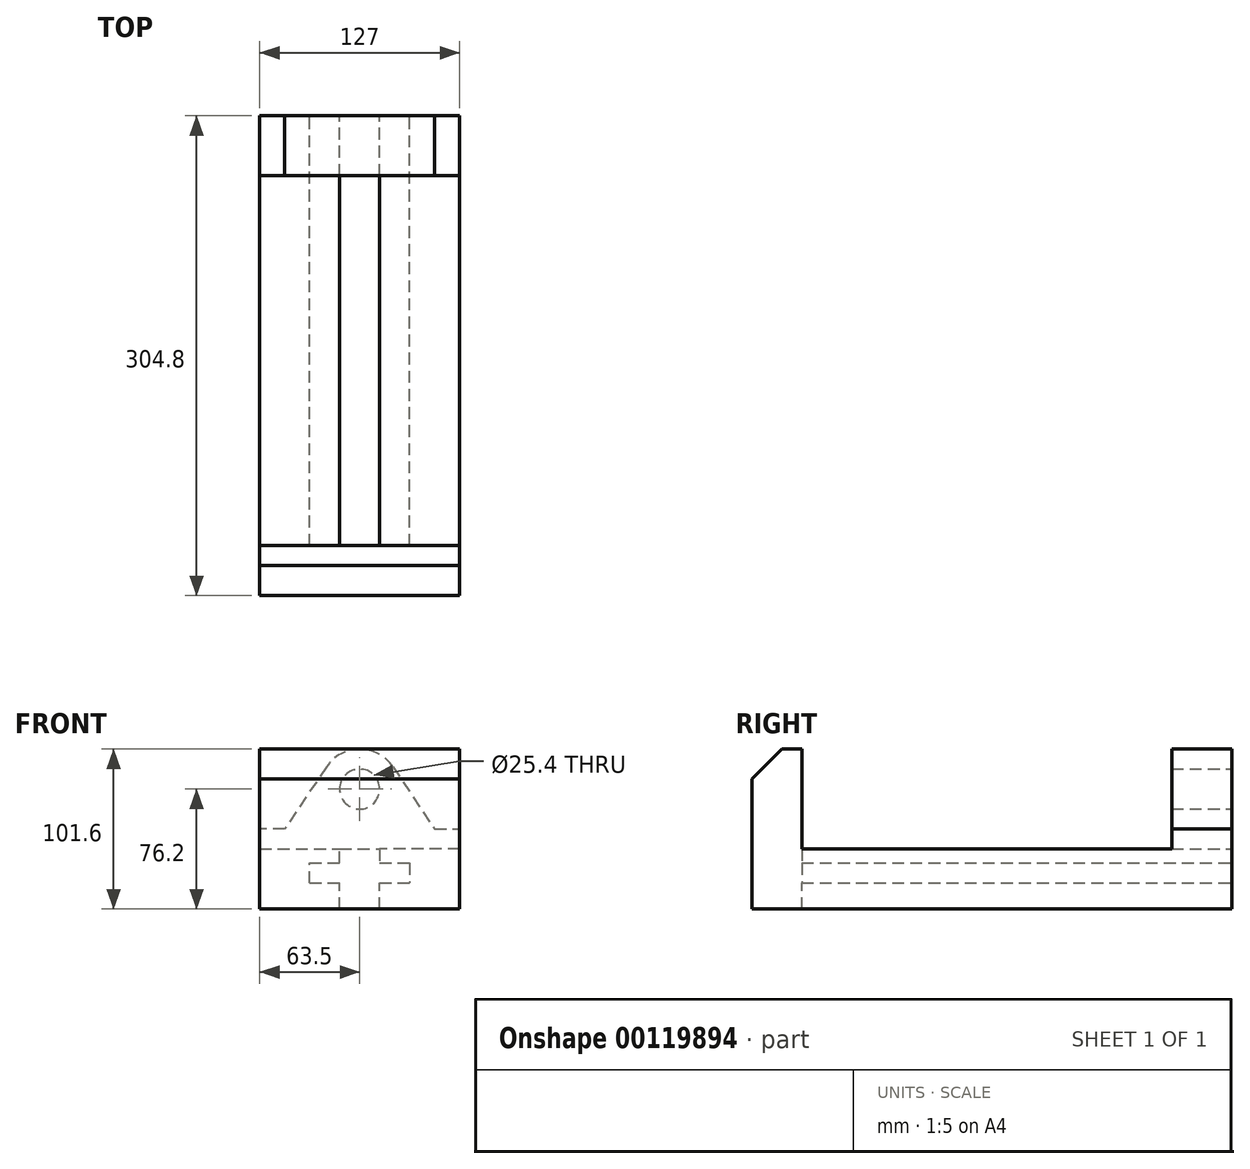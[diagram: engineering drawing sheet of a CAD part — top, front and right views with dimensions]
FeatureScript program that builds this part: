
annotation { "Feature Type Name" : "Feature", "Feature Type Description" : "" }
export const myFeature = defineFeature(function(context is Context, id is Id, definition is map)
    precondition{}
    {
        {
            var Q0;
            Q0=qCreatedBy(makeId("Front.planeOp"),FACE);
            var sketch = newSketch(context, id + "F0", { "sketchPlane" : qUnion([Q0])});
            skLineSegment(sketch, "E0.bottom", {"start": v(-63.5, 0) * mm, "end": v(63.5, 0) * mm});
            skLineSegment(sketch, "E0.left", {"start": v(-63.5, 0) * mm, "end": v(-63.5, 50.8) * mm});
            skLineSegment(sketch, "E0.right", {"start": v(63.5, 0) * mm, "end": v(63.5, 50.8) * mm});
            skPoint(sketch, "E1", {"position": v(0, 101.6) * mm});
            skArc(sketch, "E2", {"start": v(21.1, 90.35) * mm, "mid": v(0, 101.6) * mm, "end": v(-21.1, 90.35) * mm});
            skCircle(sketch, "E3", {"center": v(0, 76.2) * mm, "radius": 12.7 * mm});
            skLineSegment(sketch, "E4", {"start": v(21.1, 90.35) * mm, "end": v(47.62, 50.8) * mm});
            skLineSegment(sketch, "E5", {"start": v(47.62, 50.8) * mm, "end": v(63.5, 50.8) * mm});
            skLineSegment(sketch, "E6", {"start": v(-21.1, 90.35) * mm, "end": v(-47.62, 50.8) * mm});
            skLineSegment(sketch, "E7", {"start": v(-47.63, 50.8) * mm, "end": v(-63.5, 50.8) * mm});
            skLineSegment(sketch, "E8", {"start": v(0, 0) * mm, "end": v(0, 101.6) * mm});
            skSolve(sketch);
        }
        {
            var Q0;
            Q0 = qSketchRegion(id + "F0", true);
            extrude(context, id + "F1", {"entities" : qUnion([Q0]), "depth" : 38.1 * mm});
        }
        {
            var Q0;
            Q0=qCreatedBy(makeId("Right.planeOp"),FACE);
            var sketch = newSketch(context, id + "F2", { "sketchPlane" : qUnion([Q0])});
            skLineSegment(sketch, "E9.bottom", {"start": v(0, 0) * mm, "end": v(-304.8, 0) * mm});
            skLineSegment(sketch, "E9.top", {"start": v(0, 38.1) * mm, "end": v(-273.05, 38.1) * mm});
            skLineSegment(sketch, "E9.left", {"start": v(0, 0) * mm, "end": v(0, 38.1) * mm});
            skLineSegment(sketch, "E9.right", {"start": v(-304.8, 0) * mm, "end": v(-304.8, 82.55) * mm});
            skLineSegment(sketch, "E10", {"start": v(-38.1, 101.6) * mm, "end": v(0, 101.6) * mm, "construction": true});
            skPoint(sketch, "E11", {"position": v(-304.8, 38.1) * mm});
            skLineSegment(sketch, "E12", {"start": v(-304.8, 82.55) * mm, "end": v(-285.75, 101.6) * mm});
            skLineSegment(sketch, "E13", {"start": v(-285.75, 101.6) * mm, "end": v(-273.05, 101.6) * mm});
            skLineSegment(sketch, "E14", {"start": v(-273.05, 101.6) * mm, "end": v(-273.05, 38.1) * mm});
            skSolve(sketch);
        }
        {
            var Q0;
            Q0 = qSketchRegion(id + "F2", true);
            extrude(context, id + "F3", {"entities" : qUnion([Q0]), "operationType" : NewBodyOperationType.ADD, "oppositeDirection" : true, "depth" : 63.5 * mm, "hasSecondDirection" : true, "secondDirectionOppositeDirection" : false, "secondDirectionDepth" : 63.5 * mm});
        }
        {
            var Q0;
            Q0=qCreatedBy(makeId("Front.planeOp"),FACE);
            var sketch = newSketch(context, id + "F4", { "sketchPlane" : qUnion([Q0])});
            skLineSegment(sketch, "E15.bottom", {"start": v(-12.7, 0) * mm, "end": v(12.7, 0) * mm});
            skLineSegment(sketch, "E15.left", {"start": v(-12.7, 0) * mm, "end": v(-12.7, 16.51) * mm});
            skLineSegment(sketch, "E15.right", {"start": v(12.7, 0) * mm, "end": v(12.7, 16.51) * mm});
            skLineSegment(sketch, "E16", {"start": v(-31.75, 16.51) * mm, "end": v(-12.7, 16.51) * mm});
            skLineSegment(sketch, "E17.trimOffspring", {"start": v(12.7, 16.51) * mm, "end": v(31.75, 16.51) * mm});
            skLineSegment(sketch, "E18", {"start": v(-31.75, 16.51) * mm, "end": v(-31.75, 29.21) * mm});
            skLineSegment(sketch, "E19", {"start": v(-31.75, 29.21) * mm, "end": v(-12.7, 29.21) * mm});
            skLineSegment(sketch, "E20", {"start": v(-12.7, 29.21) * mm, "end": v(-12.7, 38.1) * mm});
            skLineSegment(sketch, "E21", {"start": v(-12.7, 38.1) * mm, "end": v(12.7, 38.1) * mm});
            skLineSegment(sketch, "E22", {"start": v(12.7, 38.1) * mm, "end": v(12.7, 29.2) * mm});
            skLineSegment(sketch, "E23", {"start": v(12.7, 29.2) * mm, "end": v(31.75, 29.21) * mm});
            skLineSegment(sketch, "E24", {"start": v(31.75, 29.21) * mm, "end": v(31.75, 16.51) * mm});
            skSolve(sketch);
        }
        {
            var Q0;
            Q0 = qSketchRegion(id + "F4", true);
            extrude(context, id + "F5", {"entities" : qUnion([Q0]), "operationType" : NewBodyOperationType.REMOVE, "depth" : 273.05 * mm});
        }
    });
